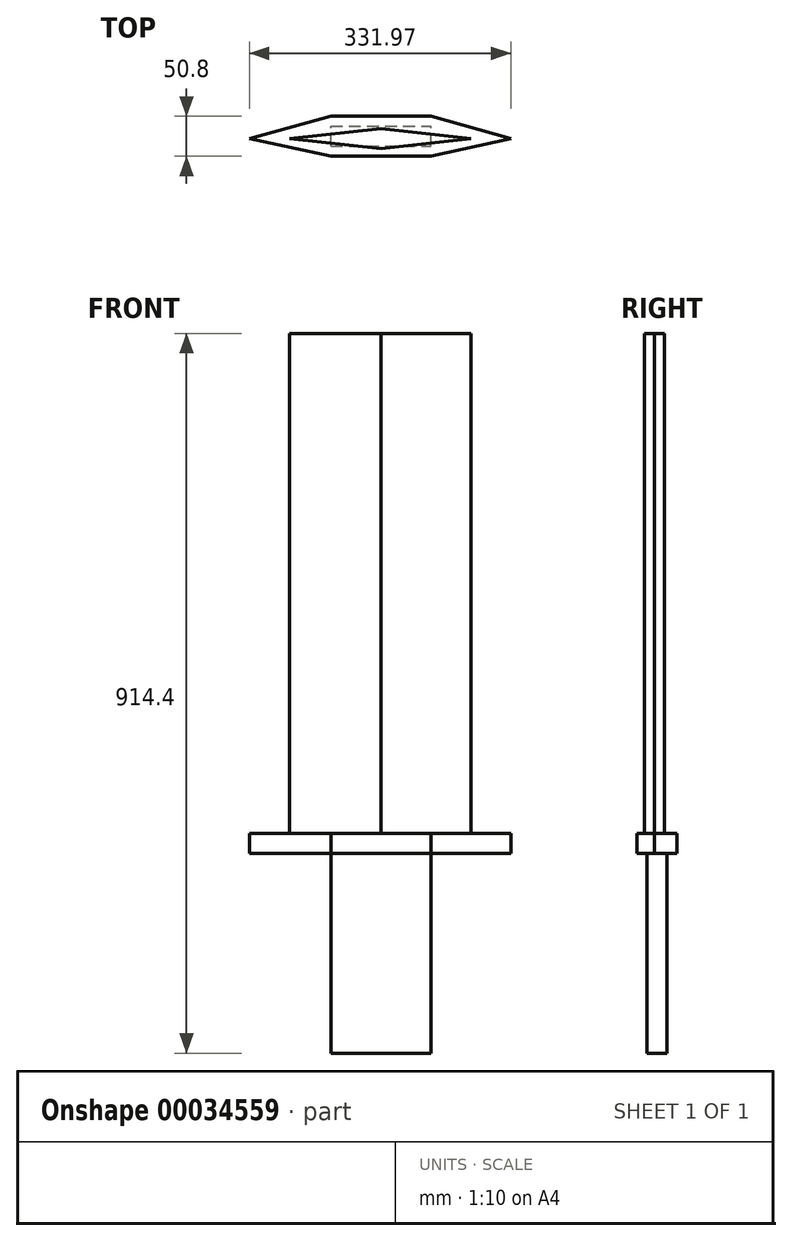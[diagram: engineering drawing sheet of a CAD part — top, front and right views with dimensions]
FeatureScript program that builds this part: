
annotation { "Feature Type Name" : "Feature", "Feature Type Description" : "" }
export const myFeature = defineFeature(function(context is Context, id is Id, definition is map)
    precondition{}
    {
        {
            var Q0;
            Q0=qCreatedBy(makeId("Top.planeOp"),FACE);
            var sketch = newSketch(context, id + "F0", { "sketchPlane" : qUnion([Q0])});
            skLineSegment(sketch, "E0.bottom", {"start": v(1.77, 28.36) * mm, "end": v(128.77, 28.36) * mm});
            skLineSegment(sketch, "E0.top", {"start": v(1.77, -22.44) * mm, "end": v(128.77, -22.44) * mm});
            skLineSegment(sketch, "E0.left", {"start": v(1.77, 28.36) * mm, "end": v(1.77, -22.44) * mm});
            skLineSegment(sketch, "E0.right", {"start": v(128.77, 28.36) * mm, "end": v(128.77, -22.44) * mm});
            skLineSegment(sketch, "E1", {"start": v(128.77, 28.36) * mm, "end": v(230.37, 0) * mm});
            skLineSegment(sketch, "E2", {"start": v(230.37, 0) * mm, "end": v(128.77, -22.44) * mm});
            skLineSegment(sketch, "E3", {"start": v(1.77, -22.44) * mm, "end": v(-101.6, 0) * mm});
            skLineSegment(sketch, "E4", {"start": v(-101.6, 0) * mm, "end": v(1.77, 28.36) * mm});
            skSolve(sketch);
        }
        {
            var Q0;
            Q0=makeQuery(id+"F0.imprint","IMPRINT",FACE,{"disambiguationData":[TD([[makeQuery(id+"F0.imprint","IMPRINT",EDGE,{"derivedFrom":sQuery(id+"F0.wireOp",EDGE,"E0.left")}),-1.0]])]});
            var Q1;
            Q1=makeQuery(id+"F0.imprint","IMPRINT",FACE,{"disambiguationData":[TD([[makeQuery(id+"F0.imprint","IMPRINT",EDGE,{"derivedFrom":sQuery(id+"F0.wireOp",EDGE,"E0.right")}),1.0]])]});
            var Q2;
            Q2=makeQuery(id+"F0.imprint","IMPRINT",FACE,{"disambiguationData":[TD([[makeQuery(id+"F0.imprint","IMPRINT",EDGE,{"derivedFrom":sQuery(id+"F0.wireOp",EDGE,"E0.bottom")}),-1.0]])]});
            extrude(context, id + "F1", {"entities" : qUnion([Q0, Q1, Q2]), "depth" : 25.4 * mm});
        }
        {
            var Q0;
            Q0=makeQuery(id+"F1.opExtrude","CAP_FACE",FACE,{"disambiguationData":[OSD([sQuery(id+"F0.wireOp",EDGE,"E0.bottom"),sQuery(id+"F0.wireOp",EDGE,"E0.top"),sQuery(id+"F0.wireOp",EDGE,"E1"),sQuery(id+"F0.wireOp",EDGE,"E2"),sQuery(id+"F0.wireOp",EDGE,"E3"),sQuery(id+"F0.wireOp",EDGE,"E4")])],"isStart":false});
            var sketch = newSketch(context, id + "F2", { "sketchPlane" : qUnion([Q0])});
            skLineSegment(sketch, "E5", {"start": v(-50.8, 0) * mm, "end": v(179.57, 0) * mm});
            skLineSegment(sketch, "E6", {"start": v(-50.8, 0) * mm, "end": v(65.27, 12.7) * mm});
            skLineSegment(sketch, "E7", {"start": v(65.27, 12.7) * mm, "end": v(179.57, 0) * mm});
            skLineSegment(sketch, "E8", {"start": v(-50.8, 0) * mm, "end": v(65.27, -12.7) * mm});
            skPoint(sketch, "E8.endSnap0", {"position": v(65.27, -22.44) * mm});
            skLineSegment(sketch, "E9", {"start": v(65.27, -12.7) * mm, "end": v(179.57, 0) * mm});
            skSolve(sketch);
        }
        {
            var Q0;
            Q0=makeQuery(id+"F2.imprint","IMPRINT",FACE,{"disambiguationData":[TD([[makeQuery(id+"F2.imprint","IMPRINT",EDGE,{"derivedFrom":sQuery(id+"F2.wireOp",EDGE,"E5")}),-1.0]])]});
            var Q1;
            Q1=makeQuery(id+"F2.imprint","IMPRINT",FACE,{"disambiguationData":[TD([[makeQuery(id+"F2.imprint","IMPRINT",EDGE,{"derivedFrom":sQuery(id+"F2.wireOp",EDGE,"E5")}),1.0]])]});
            extrude(context, id + "F3", {"entities" : qUnion([Q0, Q1]), "operationType" : NewBodyOperationType.ADD, "depth" : 635 * mm});
        }
        {
            var Q0;
            Q0=makeQuery(id+"F1.opExtrude","CAP_FACE",FACE,{"disambiguationData":[OSD([sQuery(id+"F0.wireOp",EDGE,"E0.bottom"),sQuery(id+"F0.wireOp",EDGE,"E0.top"),sQuery(id+"F0.wireOp",EDGE,"E1"),sQuery(id+"F0.wireOp",EDGE,"E2"),sQuery(id+"F0.wireOp",EDGE,"E3"),sQuery(id+"F0.wireOp",EDGE,"E4")])],"isStart":true});
            var sketch = newSketch(context, id + "F4", { "sketchPlane" : qUnion([Q0])});
            skLineSegment(sketch, "E10", {"start": v(1.77, 22.44) * mm, "end": v(1.77, 9.74) * mm});
            skLineSegment(sketch, "E11", {"start": v(128.77, -28.36) * mm, "end": v(128.77, -15.66) * mm});
            skLineSegment(sketch, "E12.bottom", {"start": v(1.77, 9.74) * mm, "end": v(128.77, 9.74) * mm});
            skLineSegment(sketch, "E12.top", {"start": v(1.77, -15.66) * mm, "end": v(128.77, -15.66) * mm});
            skLineSegment(sketch, "E12.left", {"start": v(1.77, 9.74) * mm, "end": v(1.77, -15.66) * mm});
            skLineSegment(sketch, "E12.right", {"start": v(128.77, 9.74) * mm, "end": v(128.77, -15.66) * mm});
            skSolve(sketch);
        }
        {
            var Q0;
            Q0=makeQuery(id+"F4.imprint","IMPRINT",FACE,{"disambiguationData":[TD([[makeQuery(id+"F4.imprint","IMPRINT",EDGE,{"derivedFrom":sQuery(id+"F4.wireOp",EDGE,"E12.bottom")}),-1.0]])]});
            extrude(context, id + "F5", {"entities" : qUnion([Q0]), "operationType" : NewBodyOperationType.ADD, "depth" : 254 * mm});
        }
    });
